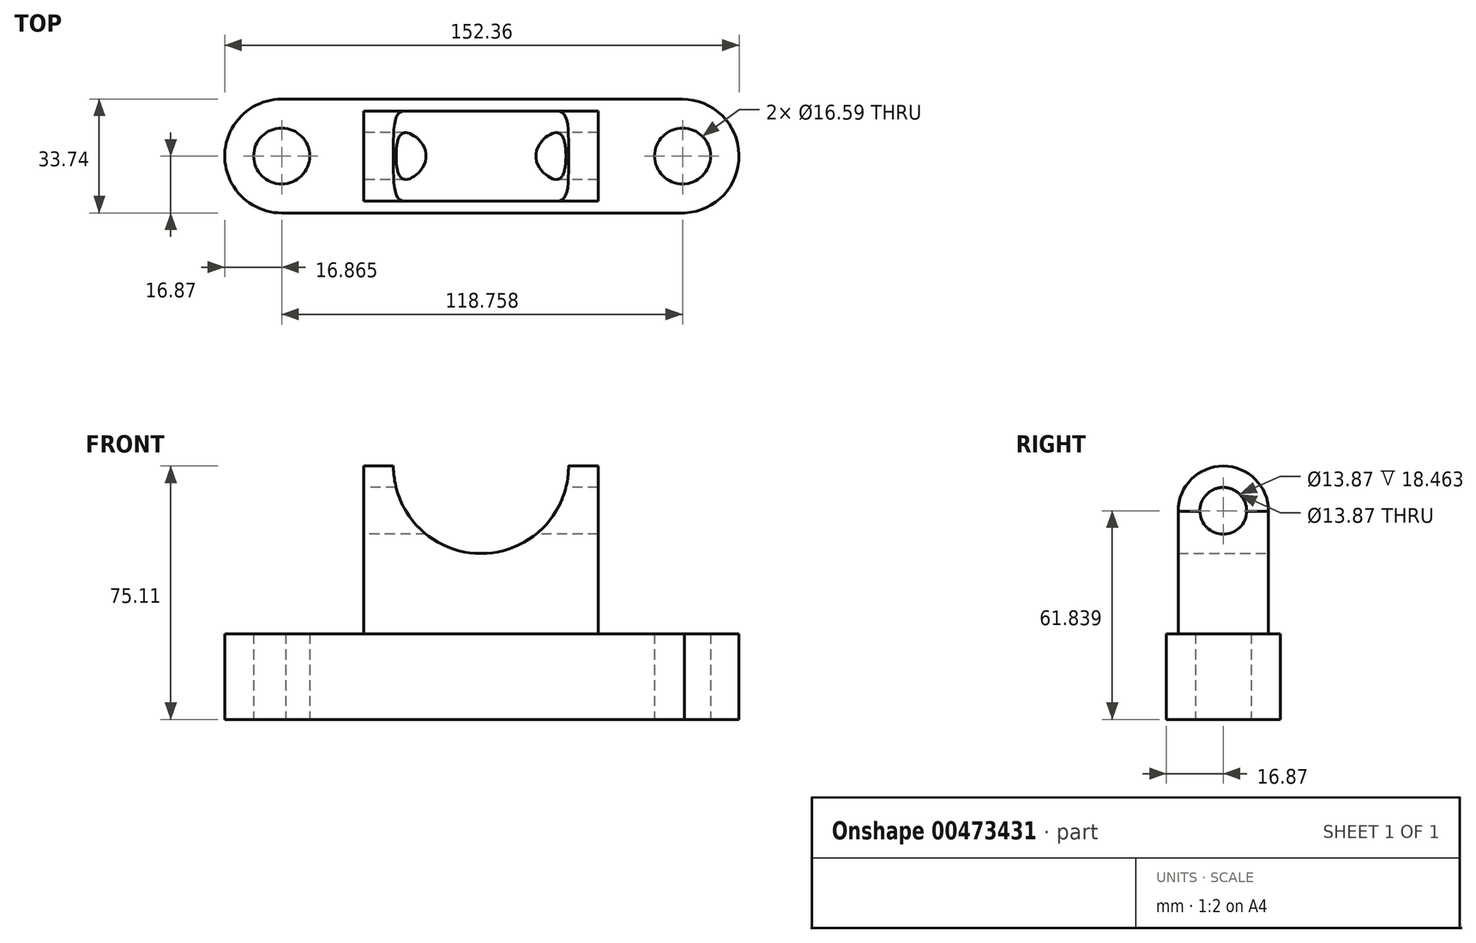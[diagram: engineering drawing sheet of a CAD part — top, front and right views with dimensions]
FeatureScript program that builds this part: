
annotation { "Feature Type Name" : "Feature", "Feature Type Description" : "" }
export const myFeature = defineFeature(function(context is Context, id is Id, definition is map)
    precondition{}
    {
        {
            var Q0;
            Q0=qCreatedBy(makeId("Top.planeOp"),FACE);
            var sketch = newSketch(context, id + "F0", { "sketchPlane" : qUnion([Q0])});
            skArc(sketch, "E0", {"start": v(-57.86, 16.82) * mm, "mid": v(-75.9, 0.6) * mm, "end": v(-59.04, -16.87) * mm});
            skArc(sketch, "E1", {"start": v(58.86, -16.85) * mm, "mid": v(76.44, -0.36) * mm, "end": v(59.57, 16.87) * mm});
            skLineSegment(sketch, "E2", {"start": v(-60.24, 16.82) * mm, "end": v(-60.24, 16.82) * mm});
            skLineSegment(sketch, "E3", {"start": v(60.3, -16.85) * mm, "end": v(-59.04, -16.87) * mm});
            skLineSegment(sketch, "E4", {"start": v(-57.86, 16.82) * mm, "end": v(59.57, 16.87) * mm});
            skLineSegment(sketch, "E5", {"start": v(-59.04, -16.87) * mm, "end": v(-59.04, -16.87) * mm});
            skSolve(sketch);
        }
        {
            var Q0;
            {var subQ1=sQuery(id+"F0.wireOp",EDGE,"E0");Q0=makeQuery(id+"F0.imprint","IMPRINT",FACE,{"disambiguationData":[TD([[makeQuery(id+"F0.imprint","IMPRINT",EDGE,{"derivedFrom":subQ1}),1.0]])]});}
            var sketch = newSketch(context, id + "F1", { "sketchPlane" : qUnion([Q0])});
            skCircle(sketch, "E6", {"center": v(-59.05, 0) * mm, "radius": 8.3 * mm});
            skCircle(sketch, "E7", {"center": v(59.71, 0) * mm, "radius": 8.3 * mm});
            skSolve(sketch);
        }
        {
            var Q0;
            Q0=makeQuery(id+"F1.imprint","IMPRINT",FACE,{"disambiguationData":[TD([[makeQuery(id+"F1.imprint","IMPRINT",EDGE,{"derivedFrom":sQuery(id+"F1.wireOp",EDGE,"E6")}),-1.0]])]});
            extrude(context, id + "F2", {"entities" : qUnion([Q0]), "depth" : 25.4 * mm});
        }
        {
            var Q0;
            Q0=makeQuery(id+"F2.opExtrude","CAP_FACE",FACE,{"disambiguationData":[OSD([sQuery(id+"F0.wireOp",EDGE,"E0"),sQuery(id+"F0.wireOp",EDGE,"E1"),sQuery(id+"F0.wireOp",EDGE,"E3"),sQuery(id+"F0.wireOp",EDGE,"E4"),sQuery(id+"F1.wireOp",EDGE,"E6"),sQuery(id+"F1.wireOp",EDGE,"E7")])],"isStart":false});
            var sketch = newSketch(context, id + "F3", { "sketchPlane" : qUnion([Q0])});
            skLineSegment(sketch, "E8.bottom", {"start": v(34.7, -13.38) * mm, "end": v(-34.7, -13.38) * mm});
            skLineSegment(sketch, "E8.top", {"start": v(34.7, 13.38) * mm, "end": v(-34.7, 13.38) * mm});
            skLineSegment(sketch, "E8.left", {"start": v(34.7, -13.38) * mm, "end": v(34.7, 13.38) * mm});
            skLineSegment(sketch, "E8.right", {"start": v(-34.7, -13.38) * mm, "end": v(-34.7, 13.38) * mm});
            skPoint(sketch, "E8.middle", {"position": v(0, 0) * mm});
            skSolve(sketch);
        }
        {
            var Q0;
            Q0=makeQuery(id+"F3.imprint","IMPRINT",FACE,{"disambiguationData":[TD([[makeQuery(id+"F3.imprint","IMPRINT",EDGE,{"derivedFrom":sQuery(id+"F3.wireOp",EDGE,"E8.bottom")}),-1.0]])]});
            extrude(context, id + "F4", {"entities" : qUnion([Q0]), "operationType" : NewBodyOperationType.ADD, "depth" : 36.32 * mm});
        }
        {
            var Q0;
            Q0=makeQuery(id+"F4.opExtrude","SWEPT_FACE",FACE,{"disambiguationData":[OSD([sQuery(id+"F3.wireOp",EDGE,"E8.right")])]});
            var sketch = newSketch(context, id + "F5", { "sketchPlane" : qUnion([Q0])});
            skCircle(sketch, "E9", {"center": v(0, 61.72) * mm, "radius": 13.38 * mm});
            skSolve(sketch);
        }
        {
            var Q0;
            {var subQ1=sQuery(id+"F3.wireOp",EDGE,"E8.right");var subQ2=makeQuery(id+"F4.opExtrude","CAP_EDGE",EDGE,{"disambiguationData":[OSD([subQ1])],"isStart":false});Q0=makeQuery(id+"F5.imprint","IMPRINT",FACE,{"disambiguationData":[TD([[makeQuery(id+"F5.imprint","IMPRINT",EDGE,{"derivedFrom":subQ2}),-1.0]])]});}
            var sketch = newSketch(context, id + "F6", { "sketchPlane" : qUnion([Q0])});
            skCircle(sketch, "E10", {"center": v(0, 61.84) * mm, "radius": 6.93 * mm});
            skSolve(sketch);
        }
        {
            var Q0;
            {var subQ1=sQuery(id+"F3.wireOp",EDGE,"E8.right");var subQ2=makeQuery(id+"F4.opExtrude","CAP_EDGE",EDGE,{"disambiguationData":[OSD([subQ1])],"isStart":false});Q0=makeQuery(id+"F5.imprint","IMPRINT",FACE,{"disambiguationData":[TD([[makeQuery(id+"F5.imprint","IMPRINT",EDGE,{"derivedFrom":subQ2}),-1.0]])]});}
            extrude(context, id + "F7", {"entities" : qUnion([Q0]), "operationType" : NewBodyOperationType.ADD, "oppositeDirection" : true, "depth" : 69.4 * mm});
        }
        {
            var Q0;
            {var subQ0=sQuery(id+"F6.wireOp",EDGE,"E10");var subQ1=makeQuery(id+"F5.imprint","IMPRINT",EDGE,{"derivedFrom":makeQuery(id+"F4.opExtrude","CAP_EDGE",EDGE,{"disambiguationData":[OSD([sQuery(id+"F3.wireOp",EDGE,"E8.right")])],"isStart":false})});var subQ2=makeQuery(id+"F6.imprint","INTERSECT",VERTEX,{"disambiguationData":[OD(0.0)],"derivedFrom":[subQ1,subQ0]});Q0=makeQuery(id+"F6.imprint","IMPRINT",FACE,{"disambiguationData":[TD([[makeQuery(id+"F6.imprint","IMPRINT",EDGE,{"disambiguationData":[TD([[subQ2,1.0]])],"derivedFrom":subQ0}),1.0]])]});}
            var Q1;
            {var subQ0=sQuery(id+"F6.wireOp",EDGE,"E10");var subQ1=makeQuery(id+"F5.imprint","IMPRINT",EDGE,{"derivedFrom":makeQuery(id+"F4.opExtrude","CAP_EDGE",EDGE,{"disambiguationData":[OSD([sQuery(id+"F3.wireOp",EDGE,"E8.right")])],"isStart":false})});var subQ2=makeQuery(id+"F6.imprint","INTERSECT",VERTEX,{"disambiguationData":[OD(0.0)],"derivedFrom":[subQ1,subQ0]});Q1=makeQuery(id+"F6.imprint","IMPRINT",FACE,{"disambiguationData":[TD([[makeQuery(id+"F6.imprint","IMPRINT",EDGE,{"disambiguationData":[TD([[subQ2,-1.0]])],"derivedFrom":subQ0}),1.0]])]});}
            extrude(context, id + "F8", {"entities" : qUnion([Q0, Q1]), "operationType" : NewBodyOperationType.REMOVE, "oppositeDirection" : true, "depth" : 100.58 * mm});
        }
        {
            var Q0;
            Q0=makeQuery(id+"F4.opExtrude","SWEPT_FACE",FACE,{"disambiguationData":[OSD([sQuery(id+"F3.wireOp",EDGE,"E8.top")])]});
            var sketch = newSketch(context, id + "F9", { "sketchPlane" : qUnion([Q0])});
            skCircle(sketch, "E11", {"center": v(0, 75.12) * mm, "radius": 25.93 * mm});
            skSolve(sketch);
        }
        {
            var Q0;
            {var subQ0=sQuery(id+"F9.wireOp",EDGE,"E11");var subQ1=sQuery(id+"F3.wireOp",EDGE,"E8.top");var subQ2=makeQuery(id+"F7.boolean.opBoolean","MERGE",EDGE,{"derivedFrom":[makeQuery(id+"F4.opExtrude","CAP_EDGE",EDGE,{"disambiguationData":[OSD([subQ1])],"isStart":false}),makeQuery(id+"F7.opExtrude","SWEPT_EDGE",EDGE,{"disambiguationData":[OSD([subQ1,sQuery(id+"F3.wireOp",EDGE,"E8.right"),sQuery(id+"F5.wireOp",EDGE,"E9")])]})]});var subQ3=makeQuery(id+"F9.imprint","INTERSECT",VERTEX,{"disambiguationData":[OD(0.0)],"derivedFrom":[subQ2,subQ0]});Q0=makeQuery(id+"F9.imprint","IMPRINT",FACE,{"disambiguationData":[TD([[makeQuery(id+"F9.imprint","IMPRINT",EDGE,{"disambiguationData":[TD([[subQ3,-1.0]])],"derivedFrom":subQ0}),1.0]])]});}
            var Q1;
            {var subQ0=sQuery(id+"F9.wireOp",EDGE,"E11");var subQ1=sQuery(id+"F3.wireOp",EDGE,"E8.top");var subQ2=makeQuery(id+"F7.boolean.opBoolean","MERGE",EDGE,{"derivedFrom":[makeQuery(id+"F4.opExtrude","CAP_EDGE",EDGE,{"disambiguationData":[OSD([subQ1])],"isStart":false}),makeQuery(id+"F7.opExtrude","SWEPT_EDGE",EDGE,{"disambiguationData":[OSD([subQ1,sQuery(id+"F3.wireOp",EDGE,"E8.right"),sQuery(id+"F5.wireOp",EDGE,"E9")])]})]});var subQ3=makeQuery(id+"F9.imprint","INTERSECT",VERTEX,{"disambiguationData":[OD(0.0)],"derivedFrom":[subQ2,subQ0]});Q1=makeQuery(id+"F9.imprint","IMPRINT",FACE,{"disambiguationData":[TD([[makeQuery(id+"F9.imprint","IMPRINT",EDGE,{"disambiguationData":[TD([[subQ3,1.0]])],"derivedFrom":subQ0}),1.0]])]});}
            extrude(context, id + "F10", {"entities" : qUnion([Q0, Q1]), "operationType" : NewBodyOperationType.REMOVE, "oppositeDirection" : true, "depth" : 29.46 * mm});
        }
    });
